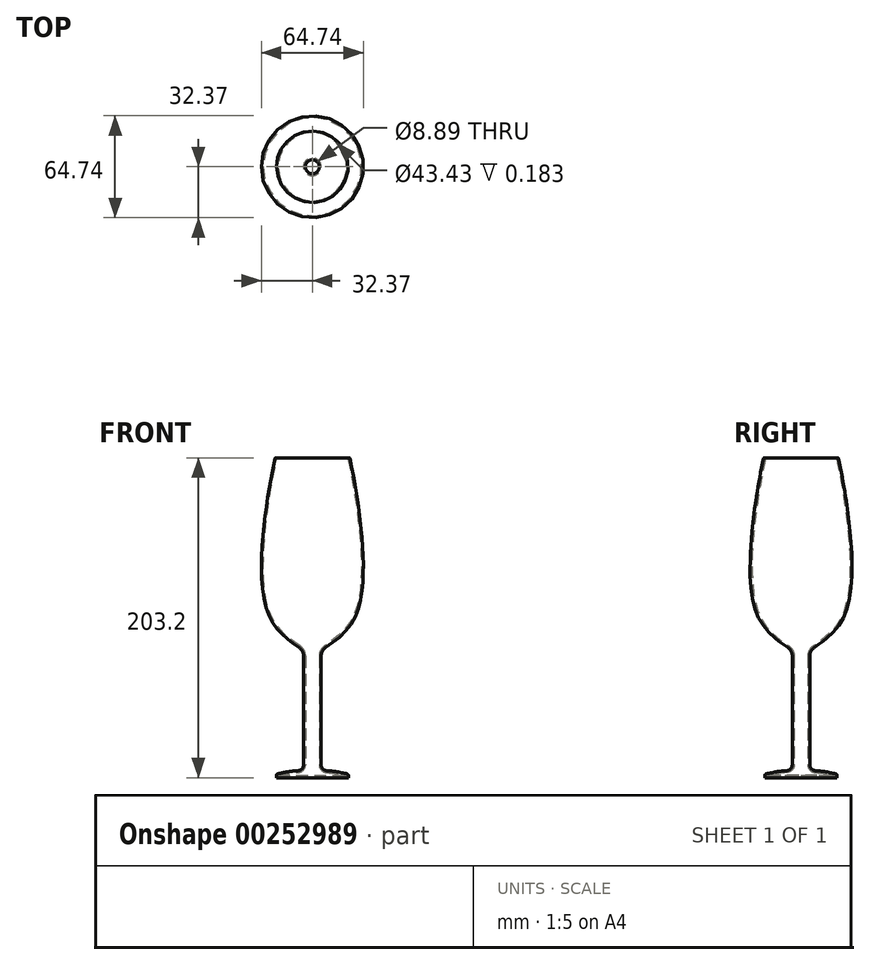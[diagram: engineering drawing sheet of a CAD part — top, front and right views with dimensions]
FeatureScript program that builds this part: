
annotation { "Feature Type Name" : "Feature", "Feature Type Description" : "" }
export const myFeature = defineFeature(function(context is Context, id is Id, definition is map)
    precondition{}
    {
        {
            var Q0;
            Q0=qCreatedBy(makeId("Front.planeOp"),FACE);
            var sketch = newSketch(context, id + "F0", { "sketchPlane" : qUnion([Q0])});
            skLineSegment(sketch, "E0", {"start": v(0, 99.75) * mm, "end": v(0, -103.45) * mm, "construction": true});
            skLineSegment(sketch, "E1", {"start": v(0, -103.45) * mm, "end": v(-22.86, -103.45) * mm});
            skLineSegment(sketch, "E2", {"start": v(-22.86, -103.45) * mm, "end": v(-22.86, -101.2) * mm});
            skFitSpline(sketch, "E3", {"points": [v(-22.86, -101.2) * mm, v(-14.73, -99.53) * mm, v(-5.59, -98.9) * mm], "startDerivative": vector(33.25, 7.55) * mm, "endDerivative": vector(21.8, -0.15) * mm});
            skLineSegment(sketch, "E4", {"start": v(-5.59, -95.18) * mm, "end": v(-5.59, -26.1) * mm});
            skFitSpline(sketch, "E5", {"points": [v(-5.59, -22.7) * mm, v(-27.8, 0) * mm, v(-30.49, 59.18) * mm, v(-23.76, 99.75) * mm], "startDerivative": vector(-92.35, 61.3) * mm, "endDerivative": vector(22.47, 113.14) * mm});
            skArc(sketch, "E6.filletArc", {"start": v(-5.59, -26.1) * mm, "mid": v(-6.33, -23.12) * mm, "end": v(-8.39, -20.84) * mm});
            skArc(sketch, "E7.filletArc", {"start": v(-9.18, -98.99) * mm, "mid": v(-6.63, -97.8) * mm, "end": v(-5.59, -95.18) * mm});
            skLineSegment(sketch, "E8", {"start": v(-5.59, -26.1) * mm, "end": v(0, -26.1) * mm});
            skLineSegment(sketch, "E9", {"start": v(0, -103.45) * mm, "end": v(0, 99.75) * mm});
            skLineSegment(sketch, "E10", {"start": v(-23.76, 99.75) * mm, "end": v(0, 99.75) * mm});
            skSolve(sketch);
        }
        {
            var Q0;
            {var subQ1=sQuery(id+"F0.wireOp",EDGE,"E1");Q0=makeQuery(id+"F0.imprint","IMPRINT",FACE,{"disambiguationData":[TD([[makeQuery(id+"F0.imprint","IMPRINT",EDGE,{"derivedFrom":subQ1}),-1.0]])]});}
            var Q1;
            Q1=makeQuery(id+"F0.imprint","IMPRINT",FACE,{"disambiguationData":[TD([[makeQuery(id+"F0.imprint","IMPRINT",EDGE,{"derivedFrom":sQuery(id+"F0.wireOp",EDGE,"E5")}),-1.0]])]});
            var Q2;
            Q2=sQuery(id+"F0.wireOp",EDGE,"E9");
            revolve(context, id + "F1", {"entities" : qUnion([Q0, Q1]), "axis" : qUnion([Q2]), "revolveType" : RevolveType.FULL});
        }
        {
            var Q0;
            Q0=makeQuery(id+"F1.opRevolve","SWEPT_FACE",FACE,{"disambiguationData":[OSD([sQuery(id+"F0.wireOp",EDGE,"E10")])]});
            shell(context, id + "F2", {"entities" : qUnion([Q0]), "thickness" : 1.14 * mm});
        }
        {
            var Q0;
            Q0=makeQuery(id+"F1.opRevolve","SWEPT_EDGE",EDGE,{"disambiguationData":[OSD([sQuery(id+"F0.wireOp",EDGE,"E5"),sQuery(id+"F0.wireOp",EDGE,"E10")])]});
            fillet(context, id + "F3", {"entities" : qUnion([Q0]), "radius" : 0.5 * mm, "tangentPropagation" : true, "allowEdgeOverflow" : false});
        }
        {
            var Q0;
            Q0=makeQuery(id+"F1.opRevolve","SWEPT_EDGE",EDGE,{"disambiguationData":[OSD([sQuery(id+"F0.wireOp",EDGE,"E2"),sQuery(id+"F0.wireOp",EDGE,"E3")])]});
            fillet(context, id + "F4", {"entities" : qUnion([Q0]), "radius" : 0.89 * mm, "tangentPropagation" : true, "allowEdgeOverflow" : false});
        }
        {
            var Q0;
            Q0=makeQuery(id+"F2.opShell","OFFSET_EDGE",EDGE,{"disambiguationData":[OSD([sQuery(id+"F0.wireOp",EDGE,"E5"),sQuery(id+"F0.wireOp",EDGE,"E10")])]});
            fillet(context, id + "F5", {"entities" : qUnion([Q0]), "radius" : 0.5 * mm, "tangentPropagation" : true, "allowEdgeOverflow" : false});
        }
    });
